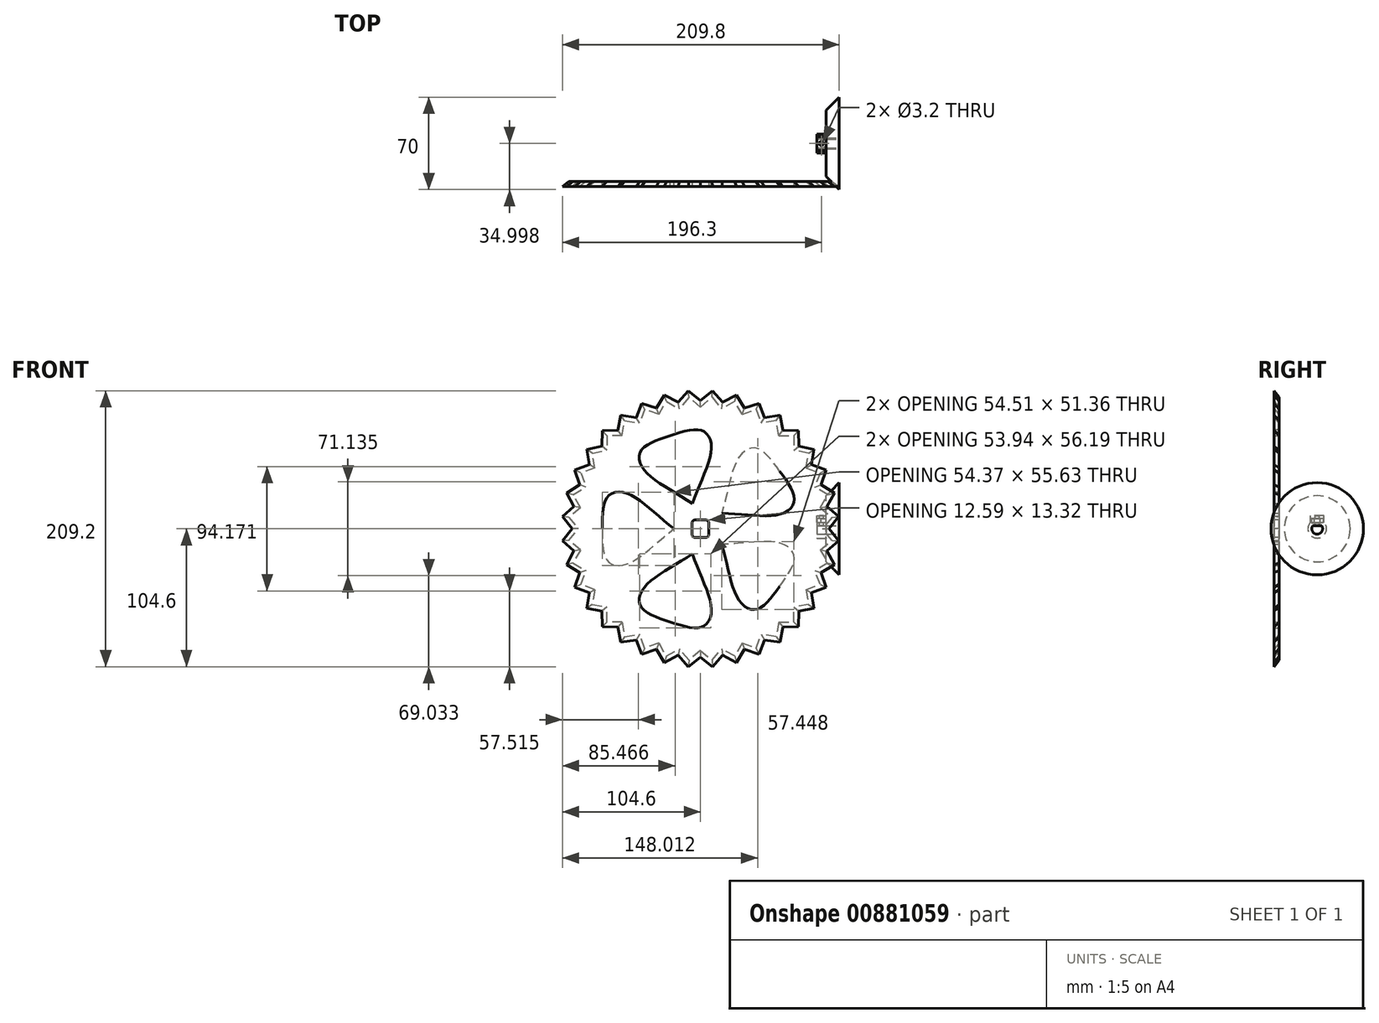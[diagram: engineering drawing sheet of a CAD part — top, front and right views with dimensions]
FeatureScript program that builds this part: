
annotation { "Feature Type Name" : "Feature", "Feature Type Description" : "" }
export const myFeature = defineFeature(function(context is Context, id is Id, definition is map)
    precondition{}
    {
        {
            var Q0;
            Q0=qCreatedBy(makeId("Front.planeOp"),FACE);
            cPlane(context, id + "F0", {"entities" : qUnion([Q0]), "cplaneType" : CPlaneType.OFFSET, "offset" : 4 * mm, "width" : 150 * mm, "height" : 150 * mm});
        }
        {
            var Q0;
            Q0=qCreatedBy(makeId("Front.planeOp"),FACE);
            var sketch = newSketch(context, id + "F1", { "sketchPlane" : qUnion([Q0])});
            skPoint(sketch, "E0.0", {"position": v(0, 0) * mm});
            skLineSegment(sketch, "E1", {"start": v(-90.9, -16.03) * mm, "end": v(-99.62, -8.72) * mm});
            skLineSegment(sketch, "E2", {"start": v(-99.62, -8.72) * mm, "end": v(-92.3, 0) * mm});
            skLineSegment(sketch, "E3.MirrorCS", {"start": v(-99.62, 8.72) * mm, "end": v(-92.3, 0) * mm});
            skLineSegment(sketch, "E4.MirrorCS", {"start": v(-90.9, 16.03) * mm, "end": v(-99.62, 8.72) * mm});
            skLineSegment(sketch, "E5.MirrorCS", {"start": v(-96.6, -25.88) * mm, "end": v(-86.74, -31.57) * mm});
            skLineSegment(sketch, "E6.MirrorCS", {"start": v(-90.63, -42.26) * mm, "end": v(-86.74, -31.57) * mm});
            skLineSegment(sketch, "E7.MirrorCS", {"start": v(-90.9, -16.03) * mm, "end": v(-96.6, -25.88) * mm});
            skLineSegment(sketch, "E8.MirrorCS", {"start": v(-79.94, -46.15) * mm, "end": v(-90.63, -42.26) * mm});
            skLineSegment(sketch, "E9.MirrorCS", {"start": v(-79.94, -46.15) * mm, "end": v(-81.92, -57.36) * mm});
            skLineSegment(sketch, "E10.MirrorCS", {"start": v(-59.33, -70.71) * mm, "end": v(-70.71, -70.71) * mm});
            skLineSegment(sketch, "E11.MirrorCS", {"start": v(-70.71, -70.71) * mm, "end": v(-70.71, -59.33) * mm});
            skLineSegment(sketch, "E12.MirrorCS", {"start": v(-79.94, 46.15) * mm, "end": v(-90.63, 42.26) * mm});
            skLineSegment(sketch, "E13.MirrorCS", {"start": v(-81.92, 57.36) * mm, "end": v(-70.71, 59.33) * mm});
            skLineSegment(sketch, "E14.MirrorCS", {"start": v(-90.9, 16.03) * mm, "end": v(-96.6, 25.88) * mm});
            skLineSegment(sketch, "E15.MirrorCS", {"start": v(-90.63, 42.26) * mm, "end": v(-86.74, 31.57) * mm});
            skLineSegment(sketch, "E16.MirrorCS", {"start": v(-79.94, 46.15) * mm, "end": v(-81.92, 57.36) * mm});
            skLineSegment(sketch, "E17.MirrorCS", {"start": v(-96.6, 25.88) * mm, "end": v(-86.74, 31.57) * mm});
            skLineSegment(sketch, "E18.MirrorCS", {"start": v(-31.57, 86.74) * mm, "end": v(-42.26, 90.63) * mm});
            skLineSegment(sketch, "E19.MirrorCS", {"start": v(-8.72, 99.62) * mm, "end": v(-16.03, 90.9) * mm});
            skLineSegment(sketch, "E20.MirrorCS", {"start": v(-57.36, 81.92) * mm, "end": v(-46.15, 79.94) * mm});
            skLineSegment(sketch, "E21.MirrorCS", {"start": v(-31.57, 86.74) * mm, "end": v(-25.88, 96.6) * mm});
            skLineSegment(sketch, "E22.MirrorCS", {"start": v(-59.33, 70.71) * mm, "end": v(-57.36, 81.92) * mm});
            skLineSegment(sketch, "E23.MirrorCS", {"start": v(-70.71, 70.71) * mm, "end": v(-70.71, 59.33) * mm});
            skLineSegment(sketch, "E24.MirrorCS", {"start": v(-59.33, 70.71) * mm, "end": v(-70.71, 70.71) * mm});
            skLineSegment(sketch, "E25.MirrorCS", {"start": v(-42.26, 90.63) * mm, "end": v(-46.15, 79.94) * mm});
            skLineSegment(sketch, "E26.MirrorCS", {"start": v(-25.88, 96.6) * mm, "end": v(-16.03, 90.9) * mm});
            skLineSegment(sketch, "E27.MirrorCS", {"start": v(0, 92.3) * mm, "end": v(-8.72, 99.62) * mm});
            skLineSegment(sketch, "E28.MirrorCS", {"start": v(79.94, 46.15) * mm, "end": v(81.92, 57.36) * mm});
            skLineSegment(sketch, "E29.MirrorCS", {"start": v(0, 92.3) * mm, "end": v(8.72, 99.62) * mm});
            skLineSegment(sketch, "E30.MirrorCS", {"start": v(96.6, 25.88) * mm, "end": v(86.74, 31.57) * mm});
            skLineSegment(sketch, "E31.MirrorCS", {"start": v(57.36, 81.92) * mm, "end": v(46.15, 79.94) * mm});
            skLineSegment(sketch, "E32.MirrorCS", {"start": v(25.88, 96.6) * mm, "end": v(16.03, 90.9) * mm});
            skLineSegment(sketch, "E33.MirrorCS", {"start": v(31.57, 86.74) * mm, "end": v(25.88, 96.6) * mm});
            skLineSegment(sketch, "E34.MirrorCS", {"start": v(59.33, 70.71) * mm, "end": v(57.36, 81.92) * mm});
            skLineSegment(sketch, "E35.MirrorCS", {"start": v(8.72, 99.62) * mm, "end": v(16.03, 90.9) * mm});
            skLineSegment(sketch, "E36.MirrorCS", {"start": v(59.33, 70.71) * mm, "end": v(70.71, 70.71) * mm});
            skLineSegment(sketch, "E37.MirrorCS", {"start": v(81.92, 57.36) * mm, "end": v(70.71, 59.33) * mm});
            skLineSegment(sketch, "E38.MirrorCS", {"start": v(42.26, 90.63) * mm, "end": v(46.15, 79.94) * mm});
            skLineSegment(sketch, "E39.MirrorCS", {"start": v(70.71, 70.71) * mm, "end": v(70.71, 59.33) * mm});
            skLineSegment(sketch, "E40.MirrorCS", {"start": v(31.57, 86.74) * mm, "end": v(42.26, 90.63) * mm});
            skLineSegment(sketch, "E41.MirrorCS", {"start": v(90.9, 16.03) * mm, "end": v(96.6, 25.88) * mm});
            skLineSegment(sketch, "E42.MirrorCS", {"start": v(79.94, 46.15) * mm, "end": v(90.63, 42.26) * mm});
            skLineSegment(sketch, "E43.MirrorCS", {"start": v(90.63, 42.26) * mm, "end": v(86.74, 31.57) * mm});
            skLineSegment(sketch, "E44.MirrorCS", {"start": v(96.6, -25.88) * mm, "end": v(86.74, -31.57) * mm});
            skLineSegment(sketch, "E45.MirrorCS", {"start": v(90.63, -42.26) * mm, "end": v(86.74, -31.57) * mm});
            skLineSegment(sketch, "E46.MirrorCS", {"start": v(79.94, -46.15) * mm, "end": v(90.63, -42.26) * mm});
            skLineSegment(sketch, "E47.MirrorCS", {"start": v(90.9, -16.03) * mm, "end": v(96.6, -25.88) * mm});
            skLineSegment(sketch, "E48.MirrorCS", {"start": v(90.9, -16.03) * mm, "end": v(99.62, -8.72) * mm});
            skLineSegment(sketch, "E49.MirrorCS", {"start": v(90.9, 16.03) * mm, "end": v(99.62, 8.72) * mm});
            skLineSegment(sketch, "E50.MirrorCS", {"start": v(99.62, 8.72) * mm, "end": v(92.3, 0) * mm});
            skLineSegment(sketch, "E51.MirrorCS", {"start": v(99.62, -8.72) * mm, "end": v(92.3, 0) * mm});
            skLineSegment(sketch, "E52.MirrorCS", {"start": v(79.94, -46.15) * mm, "end": v(81.92, -57.36) * mm});
            skLineSegment(sketch, "E53.MirrorCS", {"start": v(57.36, -81.92) * mm, "end": v(46.15, -79.94) * mm});
            skLineSegment(sketch, "E54.MirrorCS", {"start": v(70.71, -70.71) * mm, "end": v(70.71, -59.33) * mm});
            skLineSegment(sketch, "E55.MirrorCS", {"start": v(81.92, -57.36) * mm, "end": v(70.71, -59.33) * mm});
            skLineSegment(sketch, "E56.MirrorCS", {"start": v(59.33, -70.71) * mm, "end": v(70.71, -70.71) * mm});
            skLineSegment(sketch, "E57.MirrorCS", {"start": v(59.33, -70.71) * mm, "end": v(57.36, -81.92) * mm});
            skLineSegment(sketch, "E58.MirrorCS", {"start": v(31.57, -86.74) * mm, "end": v(25.88, -96.6) * mm});
            skLineSegment(sketch, "E59.MirrorCS", {"start": v(31.57, -86.74) * mm, "end": v(42.26, -90.63) * mm});
            skLineSegment(sketch, "E60.MirrorCS", {"start": v(42.26, -90.63) * mm, "end": v(46.15, -79.94) * mm});
            skLineSegment(sketch, "E61.MirrorCS", {"start": v(8.72, -99.62) * mm, "end": v(16.03, -90.9) * mm});
            skLineSegment(sketch, "E62.MirrorCS", {"start": v(25.88, -96.6) * mm, "end": v(16.03, -90.9) * mm});
            skLineSegment(sketch, "E63.MirrorCS", {"start": v(0, -92.3) * mm, "end": v(8.72, -99.62) * mm});
            skLineSegment(sketch, "E64.MirrorCS", {"start": v(0, -92.3) * mm, "end": v(-8.72, -99.62) * mm});
            skLineSegment(sketch, "E65.MirrorCS", {"start": v(-8.72, -99.62) * mm, "end": v(-16.03, -90.9) * mm});
            skLineSegment(sketch, "E66.MirrorCS", {"start": v(-25.88, -96.6) * mm, "end": v(-16.03, -90.9) * mm});
            skLineSegment(sketch, "E67.MirrorCS", {"start": v(-31.57, -86.74) * mm, "end": v(-42.26, -90.63) * mm});
            skLineSegment(sketch, "E68.MirrorCS", {"start": v(-42.26, -90.63) * mm, "end": v(-46.15, -79.94) * mm});
            skLineSegment(sketch, "E69.MirrorCS", {"start": v(-31.57, -86.74) * mm, "end": v(-25.88, -96.6) * mm});
            skLineSegment(sketch, "E70.MirrorCS", {"start": v(-59.33, -70.71) * mm, "end": v(-57.36, -81.92) * mm});
            skLineSegment(sketch, "E71.MirrorCS", {"start": v(-57.36, -81.92) * mm, "end": v(-46.15, -79.94) * mm});
            skLineSegment(sketch, "E72", {"start": v(-81.92, -57.36) * mm, "end": v(-70.71, -59.33) * mm});
            skSolve(sketch);
        }
        {
            var Q0;
            Q0=qCreatedBy(id+"F0.planeOp",FACE);
            var sketch = newSketch(context, id + "F2", { "sketchPlane" : qUnion([Q0])});
            skLineSegment(sketch, "E73.0.0", {"start": v(-48.65, 84.27) * mm, "end": v(-60.23, 86.01) * mm});
            skLineSegment(sketch, "E73.0.1", {"start": v(-60.23, 86.01) * mm, "end": v(-62.55, 74.54) * mm});
            skLineSegment(sketch, "E73.0.2", {"start": v(-62.55, 74.54) * mm, "end": v(-74.25, 74.25) * mm});
            skLineSegment(sketch, "E73.0.3", {"start": v(-74.25, 74.25) * mm, "end": v(-74.54, 62.55) * mm});
            skLineSegment(sketch, "E73.0.4", {"start": v(-74.54, 62.55) * mm, "end": v(-86.01, 60.23) * mm});
            skLineSegment(sketch, "E73.0.5", {"start": v(-86.01, 60.23) * mm, "end": v(-84.27, 48.65) * mm});
            skLineSegment(sketch, "E73.0.6", {"start": v(-84.27, 48.65) * mm, "end": v(-95.16, 44.37) * mm});
            skLineSegment(sketch, "E73.0.7", {"start": v(-95.16, 44.37) * mm, "end": v(-91.44, 33.28) * mm});
            skLineSegment(sketch, "E73.0.8", {"start": v(-91.44, 33.28) * mm, "end": v(-101.42, 27.18) * mm});
            skLineSegment(sketch, "E73.0.9", {"start": v(-101.42, 27.18) * mm, "end": v(-95.83, 16.9) * mm});
            skLineSegment(sketch, "E73.0.10", {"start": v(-95.83, 16.9) * mm, "end": v(-104.6, 9.15) * mm});
            skLineSegment(sketch, "E73.0.11", {"start": v(-104.6, 9.15) * mm, "end": v(-97.3, 0) * mm});
            skLineSegment(sketch, "E73.0.12", {"start": v(-97.3, 0) * mm, "end": v(-104.6, -9.15) * mm});
            skLineSegment(sketch, "E73.0.13", {"start": v(-104.6, -9.15) * mm, "end": v(-95.83, -16.9) * mm});
            skLineSegment(sketch, "E73.0.14", {"start": v(-95.83, -16.9) * mm, "end": v(-101.42, -27.18) * mm});
            skLineSegment(sketch, "E73.0.15", {"start": v(-101.42, -27.18) * mm, "end": v(-91.44, -33.28) * mm});
            skLineSegment(sketch, "E73.0.16", {"start": v(-91.44, -33.28) * mm, "end": v(-95.16, -44.37) * mm});
            skLineSegment(sketch, "E73.0.17", {"start": v(-95.16, -44.37) * mm, "end": v(-84.27, -48.65) * mm});
            skLineSegment(sketch, "E73.0.18", {"start": v(-84.27, -48.65) * mm, "end": v(-86.01, -60.23) * mm});
            skLineSegment(sketch, "E73.0.19", {"start": v(-86.01, -60.23) * mm, "end": v(-74.54, -62.55) * mm});
            skLineSegment(sketch, "E73.0.20", {"start": v(-74.54, -62.55) * mm, "end": v(-74.25, -74.25) * mm});
            skLineSegment(sketch, "E73.0.21", {"start": v(-74.25, -74.25) * mm, "end": v(-62.55, -74.54) * mm});
            skLineSegment(sketch, "E73.0.22", {"start": v(-62.55, -74.54) * mm, "end": v(-60.23, -86.01) * mm});
            skLineSegment(sketch, "E73.0.23", {"start": v(-60.23, -86.01) * mm, "end": v(-48.65, -84.27) * mm});
            skLineSegment(sketch, "E73.0.24", {"start": v(-48.65, -84.27) * mm, "end": v(-44.37, -95.16) * mm});
            skLineSegment(sketch, "E73.0.25", {"start": v(-44.37, -95.16) * mm, "end": v(-33.28, -91.44) * mm});
            skLineSegment(sketch, "E73.0.26", {"start": v(-33.28, -91.44) * mm, "end": v(-27.18, -101.42) * mm});
            skLineSegment(sketch, "E73.0.27", {"start": v(-27.18, -101.42) * mm, "end": v(-16.9, -95.83) * mm});
            skLineSegment(sketch, "E73.0.28", {"start": v(-16.9, -95.83) * mm, "end": v(-9.15, -104.6) * mm});
            skLineSegment(sketch, "E73.0.29", {"start": v(-9.15, -104.6) * mm, "end": v(0, -97.3) * mm});
            skLineSegment(sketch, "E73.0.30", {"start": v(0, -97.3) * mm, "end": v(9.15, -104.6) * mm});
            skLineSegment(sketch, "E73.0.31", {"start": v(9.15, -104.6) * mm, "end": v(16.9, -95.83) * mm});
            skLineSegment(sketch, "E73.0.32", {"start": v(16.9, -95.83) * mm, "end": v(27.18, -101.42) * mm});
            skLineSegment(sketch, "E73.0.33", {"start": v(27.18, -101.42) * mm, "end": v(33.28, -91.44) * mm});
            skLineSegment(sketch, "E73.0.34", {"start": v(33.28, -91.44) * mm, "end": v(44.37, -95.16) * mm});
            skLineSegment(sketch, "E73.0.35", {"start": v(44.37, -95.16) * mm, "end": v(48.65, -84.27) * mm});
            skLineSegment(sketch, "E73.0.36", {"start": v(48.65, -84.27) * mm, "end": v(60.23, -86.01) * mm});
            skLineSegment(sketch, "E73.0.37", {"start": v(60.23, -86.01) * mm, "end": v(62.55, -74.54) * mm});
            skLineSegment(sketch, "E73.0.38", {"start": v(62.55, -74.54) * mm, "end": v(74.25, -74.25) * mm});
            skLineSegment(sketch, "E73.0.39", {"start": v(74.25, -74.25) * mm, "end": v(74.54, -62.55) * mm});
            skLineSegment(sketch, "E73.0.40", {"start": v(74.54, -62.55) * mm, "end": v(86.01, -60.23) * mm});
            skLineSegment(sketch, "E73.0.41", {"start": v(86.01, -60.23) * mm, "end": v(84.27, -48.65) * mm});
            skLineSegment(sketch, "E73.0.42", {"start": v(84.27, -48.65) * mm, "end": v(95.16, -44.37) * mm});
            skLineSegment(sketch, "E73.0.43", {"start": v(95.16, -44.37) * mm, "end": v(91.44, -33.28) * mm});
            skLineSegment(sketch, "E73.0.44", {"start": v(91.44, -33.28) * mm, "end": v(101.42, -27.18) * mm});
            skLineSegment(sketch, "E73.0.45", {"start": v(101.42, -27.18) * mm, "end": v(95.83, -16.9) * mm});
            skLineSegment(sketch, "E73.0.46", {"start": v(95.83, -16.9) * mm, "end": v(104.6, -9.15) * mm});
            skLineSegment(sketch, "E73.0.47", {"start": v(104.6, -9.15) * mm, "end": v(97.3, 0) * mm});
            skLineSegment(sketch, "E73.0.48", {"start": v(97.3, 0) * mm, "end": v(104.6, 9.15) * mm});
            skLineSegment(sketch, "E73.0.49", {"start": v(104.6, 9.15) * mm, "end": v(95.83, 16.9) * mm});
            skLineSegment(sketch, "E73.0.50", {"start": v(95.83, 16.9) * mm, "end": v(101.42, 27.18) * mm});
            skLineSegment(sketch, "E73.0.51", {"start": v(101.42, 27.18) * mm, "end": v(91.44, 33.28) * mm});
            skLineSegment(sketch, "E73.0.52", {"start": v(91.44, 33.28) * mm, "end": v(95.16, 44.37) * mm});
            skLineSegment(sketch, "E73.0.53", {"start": v(95.16, 44.37) * mm, "end": v(84.27, 48.65) * mm});
            skLineSegment(sketch, "E73.0.54", {"start": v(84.27, 48.65) * mm, "end": v(86.01, 60.23) * mm});
            skLineSegment(sketch, "E73.0.55", {"start": v(86.01, 60.23) * mm, "end": v(74.54, 62.55) * mm});
            skLineSegment(sketch, "E73.0.56", {"start": v(74.54, 62.55) * mm, "end": v(74.25, 74.25) * mm});
            skLineSegment(sketch, "E73.0.57", {"start": v(74.25, 74.25) * mm, "end": v(62.55, 74.54) * mm});
            skLineSegment(sketch, "E73.0.58", {"start": v(62.55, 74.54) * mm, "end": v(60.23, 86.01) * mm});
            skLineSegment(sketch, "E73.0.59", {"start": v(60.23, 86.01) * mm, "end": v(48.65, 84.27) * mm});
            skLineSegment(sketch, "E73.0.60", {"start": v(48.65, 84.27) * mm, "end": v(44.37, 95.16) * mm});
            skLineSegment(sketch, "E73.0.61", {"start": v(44.37, 95.16) * mm, "end": v(33.28, 91.44) * mm});
            skLineSegment(sketch, "E73.0.62", {"start": v(33.28, 91.44) * mm, "end": v(27.18, 101.42) * mm});
            skLineSegment(sketch, "E73.0.63", {"start": v(27.18, 101.42) * mm, "end": v(16.9, 95.83) * mm});
            skLineSegment(sketch, "E73.0.64", {"start": v(16.9, 95.83) * mm, "end": v(9.15, 104.6) * mm});
            skLineSegment(sketch, "E73.0.65", {"start": v(9.15, 104.6) * mm, "end": v(0, 97.3) * mm});
            skLineSegment(sketch, "E73.0.66", {"start": v(0, 97.3) * mm, "end": v(-9.15, 104.6) * mm});
            skLineSegment(sketch, "E73.0.67", {"start": v(-9.15, 104.6) * mm, "end": v(-16.9, 95.83) * mm});
            skLineSegment(sketch, "E73.0.68", {"start": v(-16.9, 95.83) * mm, "end": v(-27.18, 101.42) * mm});
            skLineSegment(sketch, "E73.0.69", {"start": v(-27.18, 101.42) * mm, "end": v(-33.28, 91.44) * mm});
            skLineSegment(sketch, "E73.0.70", {"start": v(-33.28, 91.44) * mm, "end": v(-44.37, 95.16) * mm});
            skLineSegment(sketch, "E73.0.71", {"start": v(-44.37, 95.16) * mm, "end": v(-48.65, 84.27) * mm});
            skSolve(sketch);
        }
        {
            var Q0;
            Q0 = qSketchRegion(id + "F1", true);
            var Q1;
            Q1 = qSketchRegion(id + "F2", true);
            loft(context, id + "F3", {"sheetProfilesArray" : [{ "sheetProfileEntities" : qUnion([Q0]) }, { "sheetProfileEntities" : qUnion([Q1]) }]});
        }
        {
            var Q0;
            Q0=qCreatedBy(makeId("Right.planeOp"),FACE);
            var sketch = newSketch(context, id + "F4", { "sketchPlane" : qUnion([Q0])});
            skCircle(sketch, "E74", {"center": v(42.33, 0) * mm, "radius": 25 * mm});
            skSolve(sketch);
        }
        {
            var Q0;
            Q0 = qSketchRegion(id + "F4", true);
            extrude(context, id + "F5", {"entities" : qUnion([Q0]), "depth" : 10 * mm, "offsetDistance" : 25 * mm, "hasDraft" : true, "draftAngle" : 45 * degree});
        }
        {
            var Q0;
            Q0=makeQuery(id+"F5.opExtrude","SWEPT_BODY",BODY,{"disambiguationData":[OSD([sQuery(id+"F4.wireOp",EDGE,"E74")])]});
            transform(context, id + "F6", {"entities" : qUnion([Q0]), "transformType" : TransformType.TRANSLATION_3D, "dx" : 95.2 * mm, "dy" : -13.6 * mm, "dz" : 0 * mm, "makeCopy" : false});
        }
        {
            var Q0;
            Q0=makeQuery(id+"F5.opExtrude","CAP_FACE",FACE,{"disambiguationData":[OSD([sQuery(id+"F4.wireOp",EDGE,"E74")])],"isStart":true});
            var sketch = newSketch(context, id + "F7", { "sketchPlane" : qUnion([Q0])});
            skLineSegment(sketch, "E75", {"start": v(-36.26, 23.84) * mm, "end": v(-37.83, 11.85) * mm});
            skLineSegment(sketch, "E76", {"start": v(-37.83, 11.85) * mm, "end": v(-49.82, 13.42) * mm});
            skLineSegment(sketch, "E77.MirrorCS", {"start": v(-28.09, 14.93) * mm, "end": v(-19.18, 23.1) * mm});
            skLineSegment(sketch, "E78.MirrorCS", {"start": v(-36.26, 23.84) * mm, "end": v(-28.09, 14.93) * mm});
            skLineSegment(sketch, "E79.MirrorCS", {"start": v(-28.73, 0) * mm, "end": v(-19.18, 23.1) * mm});
            skLineSegment(sketch, "E80.MirrorCS", {"start": v(-53.51, -3.28) * mm, "end": v(-41.98, -6.9) * mm});
            skLineSegment(sketch, "E81.MirrorCS", {"start": v(-41.98, -6.9) * mm, "end": v(-45.6, -18.44) * mm});
            skLineSegment(sketch, "E82.MirrorCS", {"start": v(-53.51, -3.28) * mm, "end": v(-43.32, 3.22) * mm});
            skLineSegment(sketch, "E83.MirrorCS", {"start": v(-43.32, 3.22) * mm, "end": v(-49.82, 13.42) * mm});
            skLineSegment(sketch, "E84.MirrorCS", {"start": v(-6.56, 11.56) * mm, "end": v(-18.64, 11.02) * mm});
            skLineSegment(sketch, "E85.MirrorCS", {"start": v(-24.22, -14.25) * mm, "end": v(-29.8, -24.98) * mm});
            skLineSegment(sketch, "E86.MirrorCS", {"start": v(-13.5, -19.82) * mm, "end": v(-24.22, -14.25) * mm});
            skLineSegment(sketch, "E87.MirrorCS", {"start": v(-16.12, -8.02) * mm, "end": v(-4.32, -5.4) * mm});
            skLineSegment(sketch, "E88.MirrorCS", {"start": v(-13.92, 1.96) * mm, "end": v(-4.32, -5.4) * mm});
            skLineSegment(sketch, "E89.MirrorCS", {"start": v(-13.5, -19.82) * mm, "end": v(-16.12, -8.02) * mm});
            skLineSegment(sketch, "E90.MirrorCS", {"start": v(-6.56, 11.56) * mm, "end": v(-13.92, 1.96) * mm});
            skLineSegment(sketch, "E91.MirrorCS", {"start": v(-18.64, 11.02) * mm, "end": v(-19.18, 23.1) * mm});
            skLineSegment(sketch, "E92.MirrorCS", {"start": v(-34.44, -13.8) * mm, "end": v(-45.6, -18.44) * mm});
            skLineSegment(sketch, "E93.MirrorCS", {"start": v(-29.8, -24.98) * mm, "end": v(-24.22, -14.25) * mm});
            skLineSegment(sketch, "E94.MirrorCS", {"start": v(-29.8, -24.98) * mm, "end": v(-34.44, -13.8) * mm});
            skSolve(sketch);
        }
        {
            var Q0;
            Q0=makeQuery(id+"F5.opExtrude","CAP_FACE",FACE,{"disambiguationData":[OSD([sQuery(id+"F4.wireOp",EDGE,"E74")])],"isStart":false});
            var sketch = newSketch(context, id + "F8", { "sketchPlane" : qUnion([Q0])});
            skPoint(sketch, "E95.0", {"position": v(28.73, 0) * mm});
            skPoint(sketch, "E96.0", {"position": v(49.82, 13.42) * mm});
            skPoint(sketch, "E97.0", {"position": v(53.51, -3.28) * mm});
            skLineSegment(sketch, "E98", {"start": v(53.51, -3.28) * mm, "end": v(28.73, 0) * mm});
            skLineSegment(sketch, "E99", {"start": v(53.51, -3.28) * mm, "end": v(63.43, -4.6) * mm});
            skPoint(sketch, "E100.0", {"position": v(44.66, 3.52) * mm});
            skLineSegment(sketch, "E101", {"start": v(58.26, 18.78) * mm, "end": v(49.73, 4.64) * mm});
            skLineSegment(sketch, "E102", {"start": v(49.73, 4.64) * mm, "end": v(63.43, -4.6) * mm});
            skLineSegment(sketch, "E103.MirrorCS", {"start": v(47.8, -9.94) * mm, "end": v(63.43, -4.6) * mm});
            skLineSegment(sketch, "E104.MirrorCS", {"start": v(52.35, -25.82) * mm, "end": v(47.8, -9.94) * mm});
            skLineSegment(sketch, "E105", {"start": v(58.26, 18.78) * mm, "end": v(49.82, 13.42) * mm});
            skLineSegment(sketch, "E106.MirrorCS", {"start": v(58.26, 18.78) * mm, "end": v(41.83, 17.05) * mm});
            skLineSegment(sketch, "E107.MirrorCS", {"start": v(41.83, 17.05) * mm, "end": v(39.28, 33.37) * mm});
            skLineSegment(sketch, "E108.MirrorCS", {"start": v(15.36, 32.35) * mm, "end": v(27.8, 21.49) * mm});
            skLineSegment(sketch, "E109.MirrorCS", {"start": v(27.8, 21.49) * mm, "end": v(39.28, 33.37) * mm});
            skPoint(sketch, "E110.MirrorP", {"position": v(45.6, -18.44) * mm});
            skLineSegment(sketch, "E111.MirrorCS", {"start": v(22.25, -20.5) * mm, "end": v(30.23, -34.97) * mm});
            skLineSegment(sketch, "E112.MirrorCS", {"start": v(36.94, -19.88) * mm, "end": v(30.23, -34.97) * mm});
            skLineSegment(sketch, "E113.MirrorCS", {"start": v(7.4, -27.75) * mm, "end": v(22.25, -20.5) * mm});
            skLineSegment(sketch, "E114.MirrorCS", {"start": v(52.35, -25.82) * mm, "end": v(36.94, -19.88) * mm});
            skLineSegment(sketch, "E115.MirrorCS", {"start": v(14.21, 15.87) * mm, "end": v(-2.3, 16.18) * mm});
            skPoint(sketch, "E116.MirrorP", {"position": v(19.18, 23.1) * mm});
            skLineSegment(sketch, "E117.MirrorCS", {"start": v(15.36, 32.35) * mm, "end": v(14.21, 15.87) * mm});
            skLineSegment(sketch, "E118.MirrorCS", {"start": v(-5.45, -7.55) * mm, "end": v(7.4, 2.82) * mm});
            skLineSegment(sketch, "E119.MirrorCS", {"start": v(7.4, 2.82) * mm, "end": v(-2.3, 16.18) * mm});
            skLineSegment(sketch, "E120.MirrorCS", {"start": v(10.58, -11.54) * mm, "end": v(-5.45, -7.55) * mm});
            skLineSegment(sketch, "E121.MirrorCS", {"start": v(7.4, -27.75) * mm, "end": v(10.58, -11.54) * mm});
            skPoint(sketch, "E122.MirrorP", {"position": v(13.5, -19.82) * mm});
            skSolve(sketch);
        }
        {
            var Q1;
            Q1=makeQuery(id+"F8.imprint","IMPRINT",FACE,{"disambiguationData":[TD([[makeQuery(id+"F8.imprint","IMPRINT",EDGE,{"derivedFrom":sQuery(id+"F8.wireOp",EDGE,"E101")}),-1.0]])]});
            var Q2;
            Q2=makeQuery(id+"F7.imprint","IMPRINT",FACE,{"disambiguationData":[TD([[makeQuery(id+"F7.imprint","IMPRINT",EDGE,{"derivedFrom":sQuery(id+"F7.wireOp",EDGE,"E75")}),1.0]])]});
            loft(context, id + "F9", {"sheetProfilesArray" : [{ "sheetProfileEntities" : qUnion([Q1]) }, { "sheetProfileEntities" : qUnion([Q2]) }]});
        }
        {
            var Q0;
            Q0=makeQuery(id+"F9.opLoft","CAP_FACE",FACE,{"disambiguationData":[OSD([makeQuery(id+"F8.imprint","IMPRINT",FACE,{"disambiguationData":[TD([[makeQuery(id+"F8.imprint","IMPRINT",EDGE,{"derivedFrom":sQuery(id+"F8.wireOp",EDGE,"E101")}),-1.0]])]})])],"isStart":true});
            var sketch = newSketch(context, id + "F10", { "sketchPlane" : qUnion([Q0])});
            skPoint(sketch, "E123.0", {"position": v(28.73, 0) * mm});
            skArc(sketch, "E124", {"start": v(25.33, 2.3) * mm, "mid": v(28.73, -4.1) * mm, "end": v(32.12, 2.3) * mm});
            skLineSegment(sketch, "E125", {"start": v(28.73, 2.3) * mm, "end": v(25.33, 2.3) * mm});
            skLineSegment(sketch, "E126", {"start": v(25.33, 2.3) * mm, "end": v(32.12, 2.3) * mm});
            skSolve(sketch);
        }
        {
            var Q0;
            Q0 = qSketchRegion(id + "F10", true);
            var Q1;
            Q1=makeQuery(id+"F9.opLoft","CAP_FACE",FACE,{"disambiguationData":[OSD([makeQuery(id+"F7.imprint","IMPRINT",FACE,{"disambiguationData":[TD([[makeQuery(id+"F7.imprint","IMPRINT",EDGE,{"derivedFrom":sQuery(id+"F7.wireOp",EDGE,"E75")}),1.0]])]})])],"isStart":true});
            extrude(context, id + "F11", {"entities" : qUnion([Q0]), "operationType" : NewBodyOperationType.REMOVE, "endBound" : BoundingType.UP_TO_SURFACE, "oppositeDirection" : true, "depth" : 25 * mm, "endBoundEntityFace" : qUnion([Q1]), "offsetDistance" : 25 * mm});
        }
        {
            var Q0;
            Q0=makeQuery(id+"F9.opLoft","CAP_FACE",FACE,{"disambiguationData":[OSD([makeQuery(id+"F7.imprint","IMPRINT",FACE,{"disambiguationData":[TD([[makeQuery(id+"F7.imprint","IMPRINT",EDGE,{"derivedFrom":sQuery(id+"F7.wireOp",EDGE,"E75")}),1.0]])]})])],"isStart":true});
            var sketch = newSketch(context, id + "F12", { "sketchPlane" : qUnion([Q0])});
            skLineSegment(sketch, "E127.0", {"start": v(-25.33, 2.3) * mm, "end": v(-32.12, 2.3) * mm});
            skArc(sketch, "E128", {"start": v(-34.02, 4.73) * mm, "mid": v(-28.73, -7.1) * mm, "end": v(-23.43, 4.73) * mm});
            skLineSegment(sketch, "E129.top", {"start": v(-32.12, 2.3) * mm, "end": v(-25.33, 2.3) * mm});
            skLineSegment(sketch, "E130.right", {"start": v(-34.02, 8.9) * mm, "end": v(-34.02, 4.73) * mm});
            skLineSegment(sketch, "E131.right", {"start": v(-23.43, 8.9) * mm, "end": v(-23.43, 4.73) * mm});
            skLineSegment(sketch, "E132", {"start": v(-28.73, 0) * mm, "end": v(-28.73, 14.62) * mm});
            skLineSegment(sketch, "E133.top", {"start": v(-34.02, 9.8) * mm, "end": v(-23.43, 9.8) * mm});
            skLineSegment(sketch, "E133.left", {"start": v(-34.02, 8.9) * mm, "end": v(-34.02, 9.8) * mm});
            skLineSegment(sketch, "E133.right", {"start": v(-23.43, 8.9) * mm, "end": v(-23.43, 9.8) * mm});
            skPoint(sketch, "E133.bottom.end.orphan", {"position": v(-32.12, 8.9) * mm});
            skArc(sketch, "E134", {"start": v(-32.24, 2.3) * mm, "mid": v(-28.73, -4.2) * mm, "end": v(-25.21, 2.3) * mm});
            skLineSegment(sketch, "E135", {"start": v(-32.24, 2.3) * mm, "end": v(-25.21, 2.3) * mm});
            skSolve(sketch);
        }
        {
            var Q0;
            Q0=makeQuery(id+"F12.imprint","IMPRINT",FACE,{"disambiguationData":[TD([[makeQuery(id+"F12.imprint","IMPRINT",EDGE,{"derivedFrom":sQuery(id+"F12.wireOp",EDGE,"E128")}),1.0]])]});
            extrude(context, id + "F13", {"entities" : qUnion([Q0]), "operationType" : NewBodyOperationType.ADD, "depth" : 7 * mm, "offsetDistance" : 25 * mm});
        }
        {
            var Q0;
            Q0=makeQuery(id+"F3.opLoft","CAP_FACE",FACE,{"disambiguationData":[OSD([makeQuery(id+"F2.imprint","IMPRINT",FACE,{"disambiguationData":[TD([[makeQuery(id+"F2.imprint","IMPRINT",EDGE,{"derivedFrom":sQuery(id+"F2.wireOp",EDGE,"E73.0.0")}),1.0]])]})])],"isStart":true});
            var sketch = newSketch(context, id + "F14", { "sketchPlane" : qUnion([Q0])});
            skLineSegment(sketch, "E136.bottom", {"start": v(6.3, -6.66) * mm, "end": v(-6.3, -6.66) * mm});
            skLineSegment(sketch, "E136.top", {"start": v(6.3, 6.66) * mm, "end": v(-6.3, 6.66) * mm});
            skLineSegment(sketch, "E136.left", {"start": v(6.3, -6.66) * mm, "end": v(6.3, 6.66) * mm});
            skLineSegment(sketch, "E136.right", {"start": v(-6.3, -6.66) * mm, "end": v(-6.3, 6.66) * mm});
            skPoint(sketch, "E136.middle", {"position": v(0, 0) * mm});
            skSolve(sketch);
        }
        {
            var Q0;
            Q0 = qSketchRegion(id + "F14", true);
            var Q1;
            Q1=makeQuery(id+"F3.opLoft","CAP_FACE",FACE,{"disambiguationData":[OSD([makeQuery(id+"F1.imprint","IMPRINT",FACE,{"disambiguationData":[TD([[makeQuery(id+"F1.imprint","IMPRINT",EDGE,{"derivedFrom":sQuery(id+"F1.wireOp",EDGE,"E1")}),-1.0]])]})])],"isStart":true});
            extrude(context, id + "F15", {"entities" : qUnion([Q0]), "operationType" : NewBodyOperationType.REMOVE, "endBound" : BoundingType.UP_TO_SURFACE, "oppositeDirection" : true, "depth" : 25 * mm, "endBoundEntityFace" : qUnion([Q1]), "offsetDistance" : 25 * mm});
        }
        {
            var Q0;
            Q0=makeQuery(id+"F15.boolean.opBoolean","COPY",EDGE,{"derivedFrom":makeQuery(id+"F15.opExtrude","SWEPT_EDGE",EDGE,{"disambiguationData":[OSD([sQuery(id+"F14.wireOp",EDGE,"E136.top"),sQuery(id+"F14.wireOp",EDGE,"E136.left")])]})});
            var Q1;
            Q1=makeQuery(id+"F15.boolean.opBoolean","COPY",EDGE,{"derivedFrom":makeQuery(id+"F15.opExtrude","SWEPT_EDGE",EDGE,{"disambiguationData":[OSD([sQuery(id+"F14.wireOp",EDGE,"E136.top"),sQuery(id+"F14.wireOp",EDGE,"E136.right")])]})});
            var Q2;
            Q2=makeQuery(id+"F15.boolean.opBoolean","COPY",EDGE,{"derivedFrom":makeQuery(id+"F15.opExtrude","SWEPT_EDGE",EDGE,{"disambiguationData":[OSD([sQuery(id+"F14.wireOp",EDGE,"E136.bottom"),sQuery(id+"F14.wireOp",EDGE,"E136.right")])]})});
            var Q3;
            Q3=makeQuery(id+"F15.boolean.opBoolean","COPY",EDGE,{"derivedFrom":makeQuery(id+"F15.opExtrude","SWEPT_EDGE",EDGE,{"disambiguationData":[OSD([sQuery(id+"F14.wireOp",EDGE,"E136.bottom"),sQuery(id+"F14.wireOp",EDGE,"E136.left")])]})});
            fillet(context, id + "F16", {"entities" : qUnion([Q0, Q1, Q2, Q3]), "radius" : 2.3 * mm, "tangentPropagation" : true, "allowEdgeOverflow" : false});
        }
        {
            var Q0;
            Q0=makeQuery(id+"F1.imprint","IMPRINT",FACE,{"disambiguationData":[TD([[makeQuery(id+"F1.imprint","IMPRINT",EDGE,{"derivedFrom":sQuery(id+"F1.wireOp",EDGE,"E1")}),-1.0]])]});
            var sketch = newSketch(context, id + "F17", { "sketchPlane" : qUnion([Q0])});
            skLineSegment(sketch, "E137", {"start": v(0, 0) * mm, "end": v(22.97, 70.7) * mm});
            skFitSpline(sketch, "E138", {"points": [v(60.14, -43.7) * mm, v(71.17, -21.45) * mm, v(60.14, -10.88) * mm, v(16.16, -11.74) * mm], "startDerivative": vector(54.51, 77.72) * mm, "endDerivative": vector(-114.14, -1.66) * mm});
            skFitSpline(sketch, "E139.MirrorCS", {"points": [v(60.14, -43.7) * mm, v(42.4, -61.06) * mm, v(28.94, -53.83) * mm, v(16.16, -11.74) * mm], "startDerivative": vector(-57.07, -75.86) * mm, "endDerivative": vector(-33.7, 109.06) * mm});
            skFitSpline(sketch, "E140.MirrorCS", {"points": [v(60.14, 43.7) * mm, v(71.17, 21.45) * mm, v(60.14, 10.88) * mm, v(16.16, 11.74) * mm], "startDerivative": vector(54.51, -77.72) * mm, "endDerivative": vector(-114.14, 1.66) * mm});
            skFitSpline(sketch, "E141.MirrorCS", {"points": [v(60.14, 43.7) * mm, v(42.4, 61.06) * mm, v(28.94, 53.83) * mm, v(16.16, 11.74) * mm], "startDerivative": vector(-57.07, 75.86) * mm, "endDerivative": vector(-33.7, -109.06) * mm});
            skFitSpline(sketch, "E142.MirrorCS", {"points": [v(-22.97, 70.7) * mm, v(1.6, 74.32) * mm, v(8.23, 60.56) * mm, v(-6.17, 19) * mm], "startDerivative": vector(90.76, 27.83) * mm, "endDerivative": vector(-36.84, -108.04) * mm});
            skFitSpline(sketch, "E143.MirrorCS", {"points": [v(-22.97, 70.7) * mm, v(-44.97, 59.19) * mm, v(-42.26, 44.15) * mm, v(-6.17, 19) * mm], "startDerivative": vector(-89.78, -30.84) * mm, "endDerivative": vector(93.31, -65.75) * mm});
            skFitSpline(sketch, "E144.MirrorCS", {"points": [v(-74.33, 0) * mm, v(-70.19, 24.48) * mm, v(-55.05, 26.54) * mm, v(-19.97, 0) * mm], "startDerivative": vector(1.58, 94.92) * mm, "endDerivative": vector(91.36, -68.43) * mm});
            skFitSpline(sketch, "E145.MirrorCS", {"points": [v(-74.33, 0) * mm, v(-70.19, -24.48) * mm, v(-55.05, -26.54) * mm, v(-19.97, 0) * mm], "startDerivative": vector(1.58, -94.92) * mm, "endDerivative": vector(91.36, 68.43) * mm});
            skFitSpline(sketch, "E146.MirrorCS", {"points": [v(-22.97, -70.7) * mm, v(1.6, -74.32) * mm, v(8.23, -60.56) * mm, v(-6.17, -19) * mm], "startDerivative": vector(90.76, -27.83) * mm, "endDerivative": vector(-36.84, 108.04) * mm});
            skFitSpline(sketch, "E147.MirrorCS", {"points": [v(-22.97, -70.7) * mm, v(-44.97, -59.19) * mm, v(-42.26, -44.15) * mm, v(-6.17, -19) * mm], "startDerivative": vector(-89.78, 30.84) * mm, "endDerivative": vector(93.31, 65.75) * mm});
            skSolve(sketch);
        }
        {
            var Q0;
            Q0 = qSketchRegion(id + "F17", true);
            var Q1;
            Q1=makeQuery(id+"F3.opLoft","SWEPT_BODY",BODY,{"disambiguationData":[OSD([makeQuery(id+"F1.imprint","IMPRINT",FACE,{"disambiguationData":[TD([[makeQuery(id+"F1.imprint","IMPRINT",EDGE,{"derivedFrom":sQuery(id+"F1.wireOp",EDGE,"E1")}),-1.0]])]}),makeQuery(id+"F2.imprint","IMPRINT",FACE,{"disambiguationData":[TD([[makeQuery(id+"F2.imprint","IMPRINT",EDGE,{"derivedFrom":sQuery(id+"F2.wireOp",EDGE,"E73.0.0")}),1.0]])]})])]});
            extrude(context, id + "F18", {"entities" : qUnion([Q0]), "operationType" : NewBodyOperationType.REMOVE, "endBound" : BoundingType.UP_TO_BODY, "depth" : 25 * mm, "endBoundEntityBody" : qUnion([Q1]), "offsetDistance" : 25 * mm});
        }
        {
            var Q0;
            Q0=makeQuery(id+"F13.opExtrude","SWEPT_FACE",FACE,{"disambiguationData":[OSD([sQuery(id+"F12.wireOp",EDGE,"E133.top")])]});
            var sketch = newSketch(context, id + "F19", { "sketchPlane" : qUnion([Q0])});
            skPoint(sketch, "E148.orphan", {"position": v(91.7, 23.43) * mm});
            skPoint(sketch, "E149.end.orphan", {"position": v(88.2, 28.73) * mm});
            skPoint(sketch, "E150.end.orphan", {"position": v(91.7, 34.02) * mm});
            skPoint(sketch, "E150.start.orphan", {"position": v(91.7, 28.73) * mm});
            skCircle(sketch, "E151", {"center": v(91.7, 28.73) * mm, "radius": 1.6 * mm});
            skSolve(sketch);
        }
        {
            var Q0;
            Q0=makeQuery(id+"F19.imprint","IMPRINT",FACE,{"disambiguationData":[TD([[makeQuery(id+"F19.imprint","IMPRINT",EDGE,{"derivedFrom":sQuery(id+"F19.wireOp",EDGE,"E151")}),1.0]])]});
            var Q1;
            Q1=makeQuery(id+"F13.boolean.opBoolean","MERGE",FACE,{"derivedFrom":[makeQuery(id+"F11.boolean.opBoolean","COPY",FACE,{"derivedFrom":makeQuery(id+"F11.opExtrude","SWEPT_FACE",FACE,{"disambiguationData":[OSD([sQuery(id+"F10.wireOp",EDGE,"E126")])]})}),makeQuery(id+"F13.opExtrude","SWEPT_FACE",FACE,{"disambiguationData":[OSD([sQuery(id+"F12.wireOp",EDGE,"E129.top")])]})]});
            extrude(context, id + "F20", {"entities" : qUnion([Q0]), "operationType" : NewBodyOperationType.REMOVE, "endBound" : BoundingType.UP_TO_SURFACE, "oppositeDirection" : true, "depth" : 25 * mm, "endBoundEntityFace" : qUnion([Q1]), "offsetDistance" : 25 * mm});
        }
        {
            var Q0;
            Q0=makeQuery(id+"F13.opExtrude","SWEPT_FACE",FACE,{"disambiguationData":[OSD([sQuery(id+"F12.wireOp",EDGE,"E133.top")])]});
            cPlane(context, id + "F21", {"entities" : qUnion([Q0]), "cplaneType" : CPlaneType.OFFSET, "offset" : 3.75 * mm, "oppositeDirection" : true, "width" : 150 * mm, "height" : 150 * mm});
        }
        {
            var Q0;
            Q0=qCreatedBy(id+"F21.planeOp",FACE);
            var sketch = newSketch(context, id + "F22", { "sketchPlane" : qUnion([Q0])});
            skLineSegment(sketch, "E152", {"start": v(91.7, 28.73) * mm, "end": v(100.93, 28.73) * mm});
            skCircle(sketch, "E153.cCircle", {"center": v(91.3, 28.73) * mm, "radius": 3.9 * mm, "construction": true});
            skLineSegment(sketch, "E153.0", {"start": v(95.2, 30.98) * mm, "end": v(95.2, 26.48) * mm});
            skLineSegment(sketch, "E153.1", {"start": v(95.2, 26.48) * mm, "end": v(91.3, 24.23) * mm});
            skLineSegment(sketch, "E153.3", {"start": v(87.4, 26.48) * mm, "end": v(87.4, 33.23) * mm});
            skLineSegment(sketch, "E153.5", {"start": v(91.3, 33.23) * mm, "end": v(95.2, 30.98) * mm});
            skPoint(sketch, "E153.0.midPoint", {"position": v(95.07, 26.78) * mm});
            skLineSegment(sketch, "E154", {"start": v(91.7, 28.73) * mm, "end": v(78.85, 28.73) * mm});
            skPoint(sketch, "E155", {"position": v(85.23, 28.73) * mm});
            skLineSegment(sketch, "E156", {"start": v(91.3, 33.23) * mm, "end": v(87.4, 33.23) * mm});
            skLineSegment(sketch, "E157.MirrorCS", {"start": v(91.3, 24.23) * mm, "end": v(87.4, 24.23) * mm});
            skLineSegment(sketch, "E158.MirrorCS", {"start": v(87.4, 30.98) * mm, "end": v(87.4, 24.23) * mm});
            skPoint(sketch, "E159.orphan", {"position": v(87.8, 30.98) * mm});
            skPoint(sketch, "E160.bottom.end.orphan", {"position": v(85.23, 33.73) * mm});
            skPoint(sketch, "E160.top.end.orphan", {"position": v(85.23, 23.73) * mm});
            skLineSegment(sketch, "E161.bottom", {"start": v(90.4, 24.23) * mm, "end": v(84.4, 24.23) * mm});
            skLineSegment(sketch, "E161.top", {"start": v(90.4, 33.23) * mm, "end": v(84.4, 33.23) * mm});
            skLineSegment(sketch, "E161.left", {"start": v(90.4, 24.23) * mm, "end": v(90.4, 33.23) * mm});
            skLineSegment(sketch, "E161.right", {"start": v(84.4, 24.23) * mm, "end": v(84.4, 33.23) * mm});
            skPoint(sketch, "E161.middle", {"position": v(87.4, 28.73) * mm});
            skSolve(sketch);
        }
        {
            var Q0;
            Q0 = qSketchRegion(id + "F22", true);
            extrude(context, id + "F23", {"entities" : qUnion([Q0]), "operationType" : NewBodyOperationType.REMOVE, "endBound" : BoundingType.SYMMETRIC, "oppositeDirection" : true, "depth" : 3 * mm, "offsetDistance" : 25 * mm, "hasSecondDirection" : true, "secondDirectionOppositeDirection" : false, "secondDirectionDepth" : 1.3 * mm});
        }
    });
